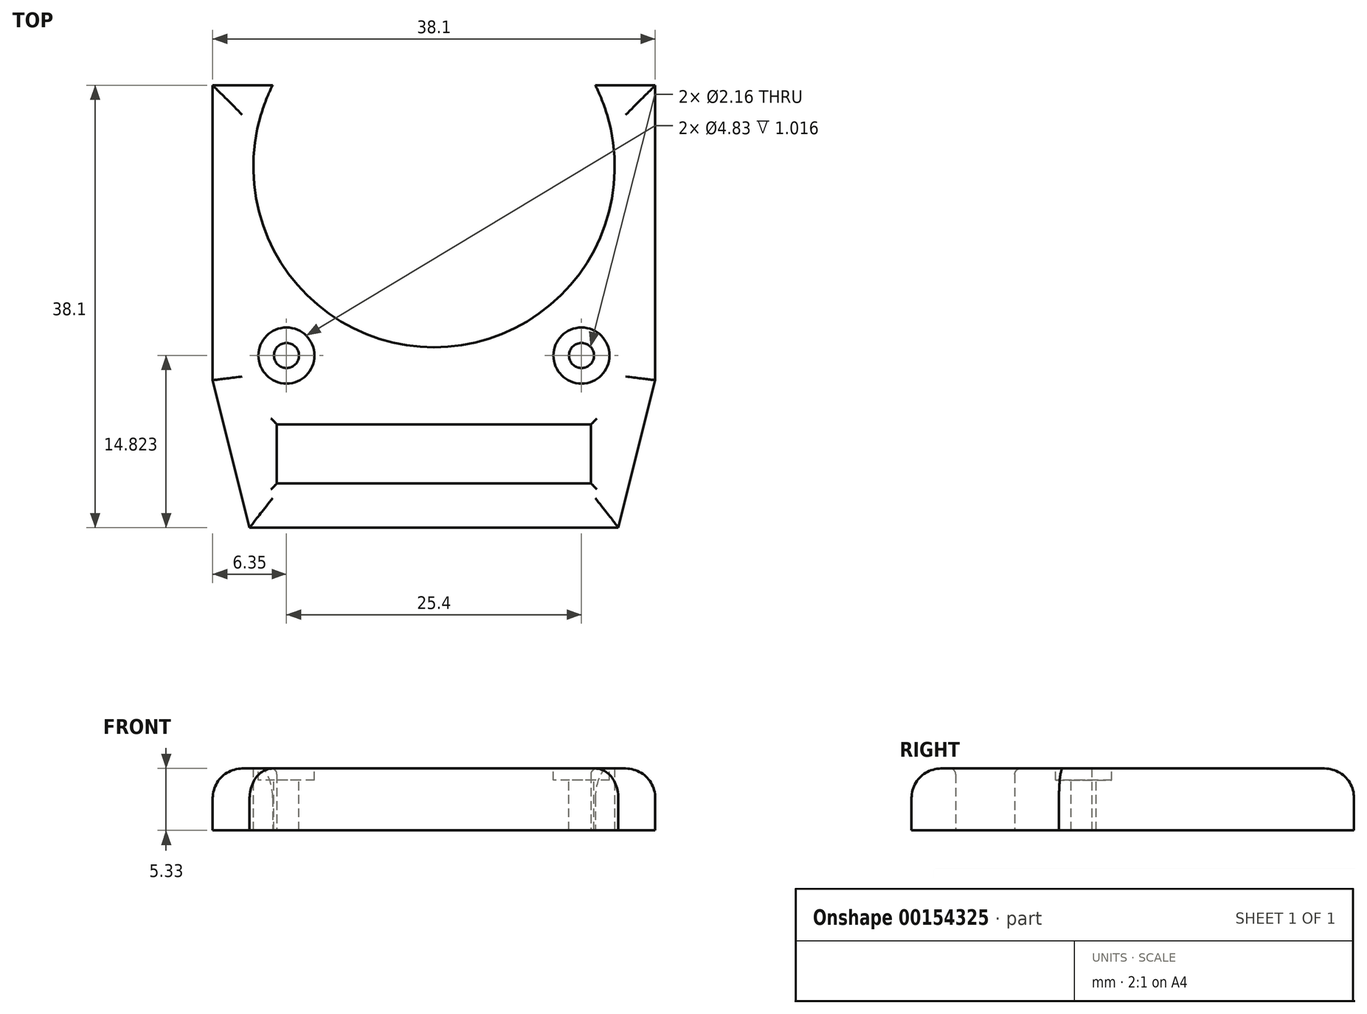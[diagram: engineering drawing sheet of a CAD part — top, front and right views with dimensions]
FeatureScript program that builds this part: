
annotation { "Feature Type Name" : "Feature", "Feature Type Description" : "" }
export const myFeature = defineFeature(function(context is Context, id is Id, definition is map)
    precondition{}
    {
        {
            var Q0;
            Q0=qCreatedBy(makeId("Top.planeOp"),FACE);
            var sketch = newSketch(context, id + "F0", { "sketchPlane" : qUnion([Q0])});
            skLineSegment(sketch, "E0.bottom", {"start": v(0, 0) * mm, "end": v(38.1, 0) * mm});
            skLineSegment(sketch, "E0.left", {"start": v(0, 0) * mm, "end": v(0, -25.4) * mm});
            skLineSegment(sketch, "E0.right", {"start": v(38.1, 0) * mm, "end": v(38.1, -25.4) * mm});
            skLineSegment(sketch, "E1.top", {"start": v(3.18, -38.1) * mm, "end": v(34.93, -38.1) * mm});
            skLineSegment(sketch, "E2", {"start": v(0, -25.4) * mm, "end": v(3.18, -38.1) * mm});
            skLineSegment(sketch, "E3", {"start": v(38.1, -25.4) * mm, "end": v(34.92, -38.1) * mm});
            skLineSegment(sketch, "E4.bottom", {"start": v(5.52, -29.21) * mm, "end": v(32.58, -29.21) * mm});
            skLineSegment(sketch, "E4.top", {"start": v(5.52, -34.3) * mm, "end": v(32.58, -34.3) * mm});
            skLineSegment(sketch, "E4.left", {"start": v(5.52, -29.21) * mm, "end": v(5.52, -34.3) * mm});
            skLineSegment(sketch, "E4.right", {"start": v(32.58, -29.21) * mm, "end": v(32.58, -34.3) * mm});
            skPoint(sketch, "E5", {"position": v(19.05, -7.01) * mm});
            skCircle(sketch, "E6", {"center": v(19.05, -7.01) * mm, "radius": 15.56 * mm});
            skPoint(sketch, "E1.bottom.start.orphan", {"position": v(3.18, -25.4) * mm});
            skSolve(sketch);
        }
        {
            var Q0;
            {var subQ0=sQuery(id+"F0.wireOp",EDGE,"E0.left");Q0=makeQuery(id+"F0.imprint","IMPRINT",FACE,{"disambiguationData":[TD([[makeQuery(id+"F0.imprint","IMPRINT",EDGE,{"derivedFrom":subQ0}),1.0]])]});}
            var Q1;
            {var subQ0=sQuery(id+"F0.wireOp",EDGE,"E6");var subQ1=sQuery(id+"F0.wireOp",EDGE,"E0.bottom");var subQ2=makeQuery(id+"F0.imprint","INTERSECT",VERTEX,{"disambiguationData":[OD(0.0)],"derivedFrom":[subQ1,subQ0]});Q1=makeQuery(id+"F0.imprint","IMPRINT",FACE,{"disambiguationData":[TD([[makeQuery(id+"F0.imprint","IMPRINT",EDGE,{"disambiguationData":[TD([[subQ2,-1.0]])],"derivedFrom":subQ1}),-1.0]])]});}
            extrude(context, id + "F1", {"entities" : qUnion([Q0, Q1]), "depth" : 6.35 * mm});
        }
        {
            var Q0;
            {var subQ0=sQuery(id+"F0.wireOp",EDGE,"E6");var subQ1=sQuery(id+"F0.wireOp",EDGE,"E0.bottom");var subQ2=makeQuery(id+"F0.imprint","INTERSECT",VERTEX,{"disambiguationData":[OD(0.0)],"derivedFrom":[subQ1,subQ0]});Q0=makeQuery(id+"F0.imprint","IMPRINT",FACE,{"disambiguationData":[TD([[makeQuery(id+"F0.imprint","IMPRINT",EDGE,{"disambiguationData":[TD([[subQ2,-1.0]])],"derivedFrom":subQ1}),-1.0]])]});}
            extrude(context, id + "F2", {"entities" : qUnion([Q0]), "operationType" : NewBodyOperationType.REMOVE, "depth" : 1.02 * mm});
        }
        {
            var Q0;
            Q0=makeQuery(id+"F1.opExtrude","CAP_FACE",FACE,{"disambiguationData":[OSD([sQuery(id+"F0.wireOp",EDGE,"E0.bottom"),sQuery(id+"F0.wireOp",EDGE,"E0.left"),sQuery(id+"F0.wireOp",EDGE,"E0.right"),sQuery(id+"F0.wireOp",EDGE,"E1.top"),sQuery(id+"F0.wireOp",EDGE,"E2"),sQuery(id+"F0.wireOp",EDGE,"E3"),sQuery(id+"F0.wireOp",EDGE,"E4.bottom"),sQuery(id+"F0.wireOp",EDGE,"E4.top"),sQuery(id+"F0.wireOp",EDGE,"E4.left"),sQuery(id+"F0.wireOp",EDGE,"E4.right")])],"isStart":false});
            var sketch = newSketch(context, id + "F3", { "sketchPlane" : qUnion([Q0])});
            skCircle(sketch, "E7", {"center": v(31.75, -23.28) * mm, "radius": 2.41 * mm});
            skCircle(sketch, "E8", {"center": v(31.75, -23.28) * mm, "radius": 1.08 * mm});
            skCircle(sketch, "E9.0", {"center": v(19.05, -7.01) * mm, "radius": 15.56 * mm});
            skCircle(sketch, "E10", {"center": v(6.35, -23.28) * mm, "radius": 2.41 * mm});
            skCircle(sketch, "E11", {"center": v(6.35, -23.28) * mm, "radius": 1.08 * mm});
            skSolve(sketch);
        }
        {
            var Q0;
            Q0=makeQuery(id+"F3.imprint","IMPRINT",FACE,{"disambiguationData":[TD([[makeQuery(id+"F3.imprint","IMPRINT",EDGE,{"derivedFrom":sQuery(id+"F3.wireOp",EDGE,"E11")}),1.0]])]});
            var Q1;
            Q1=makeQuery(id+"F3.imprint","IMPRINT",FACE,{"disambiguationData":[TD([[makeQuery(id+"F3.imprint","IMPRINT",EDGE,{"derivedFrom":sQuery(id+"F3.wireOp",EDGE,"E8")}),1.0]])]});
            var Q2;
            Q2=sQuery(id+"F3.wireOp",EDGE,"E11");
            var Q3;
            Q3=sQuery(id+"F3.wireOp",EDGE,"E8");
            extrude(context, id + "F4", {"entities" : qUnion([Q0, Q1]), "operationType" : NewBodyOperationType.REMOVE, "surfaceEntities" : qUnion([Q2, Q3]), "endBound" : BoundingType.THROUGH_ALL, "oppositeDirection" : true, "depth" : 25.4 * mm});
        }
        {
            var Q0;
            Q0=makeQuery(id+"F3.imprint","IMPRINT",FACE,{"disambiguationData":[TD([[makeQuery(id+"F3.imprint","IMPRINT",EDGE,{"derivedFrom":sQuery(id+"F3.wireOp",EDGE,"E7")}),1.0]])]});
            var Q1;
            Q1=makeQuery(id+"F3.imprint","IMPRINT",FACE,{"disambiguationData":[TD([[makeQuery(id+"F3.imprint","IMPRINT",EDGE,{"derivedFrom":sQuery(id+"F3.wireOp",EDGE,"E10")}),1.0]])]});
            extrude(context, id + "F5", {"entities" : qUnion([Q0, Q1]), "operationType" : NewBodyOperationType.REMOVE, "oppositeDirection" : true, "depth" : 1.02 * mm});
        }
        {
            var Q0;
            Q0=makeQuery(id+"F1.opExtrude","CAP_EDGE",EDGE,{"disambiguationData":[OSD([sQuery(id+"F0.wireOp",EDGE,"E0.right")])],"isStart":false});
            var Q1;
            Q1=makeQuery(id+"F1.opExtrude","CAP_EDGE",EDGE,{"disambiguationData":[OSD([sQuery(id+"F0.wireOp",EDGE,"E3")])],"isStart":false});
            var Q2;
            Q2=makeQuery(id+"F1.opExtrude","CAP_EDGE",EDGE,{"disambiguationData":[OSD([sQuery(id+"F0.wireOp",EDGE,"E1.top")])],"isStart":false});
            var Q3;
            Q3=makeQuery(id+"F1.opExtrude","CAP_EDGE",EDGE,{"disambiguationData":[OSD([sQuery(id+"F0.wireOp",EDGE,"E2")])],"isStart":false});
            var Q4;
            Q4=makeQuery(id+"F1.opExtrude","CAP_EDGE",EDGE,{"disambiguationData":[OSD([sQuery(id+"F0.wireOp",EDGE,"E0.left")])],"isStart":false});
            var Q5;
            Q5=makeQuery(id+"F1.opExtrude","CAP_EDGE",EDGE,{"disambiguationData":[OSD([sQuery(id+"F0.wireOp",EDGE,"E0.bottom")])],"isStart":false});
            fillet(context, id + "F6", {"entities" : qUnion([Q0, Q1, Q2, Q3, Q4, Q5]), "radius" : 2.54 * mm, "tangentPropagation" : true, "allowEdgeOverflow" : false});
        }
        {
            var Q0;
            Q0=makeQuery(id+"F1.opExtrude","CAP_EDGE",EDGE,{"disambiguationData":[OSD([sQuery(id+"F0.wireOp",EDGE,"E4.left")])],"isStart":false});
            var Q1;
            Q1=makeQuery(id+"F1.opExtrude","CAP_EDGE",EDGE,{"disambiguationData":[OSD([sQuery(id+"F0.wireOp",EDGE,"E4.top")])],"isStart":false});
            var Q2;
            Q2=makeQuery(id+"F1.opExtrude","CAP_EDGE",EDGE,{"disambiguationData":[OSD([sQuery(id+"F0.wireOp",EDGE,"E4.bottom")])],"isStart":false});
            var Q3;
            Q3=makeQuery(id+"F1.opExtrude","CAP_EDGE",EDGE,{"disambiguationData":[OSD([sQuery(id+"F0.wireOp",EDGE,"E4.right")])],"isStart":false});
            fillet(context, id + "F7", {"entities" : qUnion([Q0, Q1, Q2, Q3]), "radius" : 0.5 * mm, "tangentPropagation" : true, "allowEdgeOverflow" : false});
        }
    });
